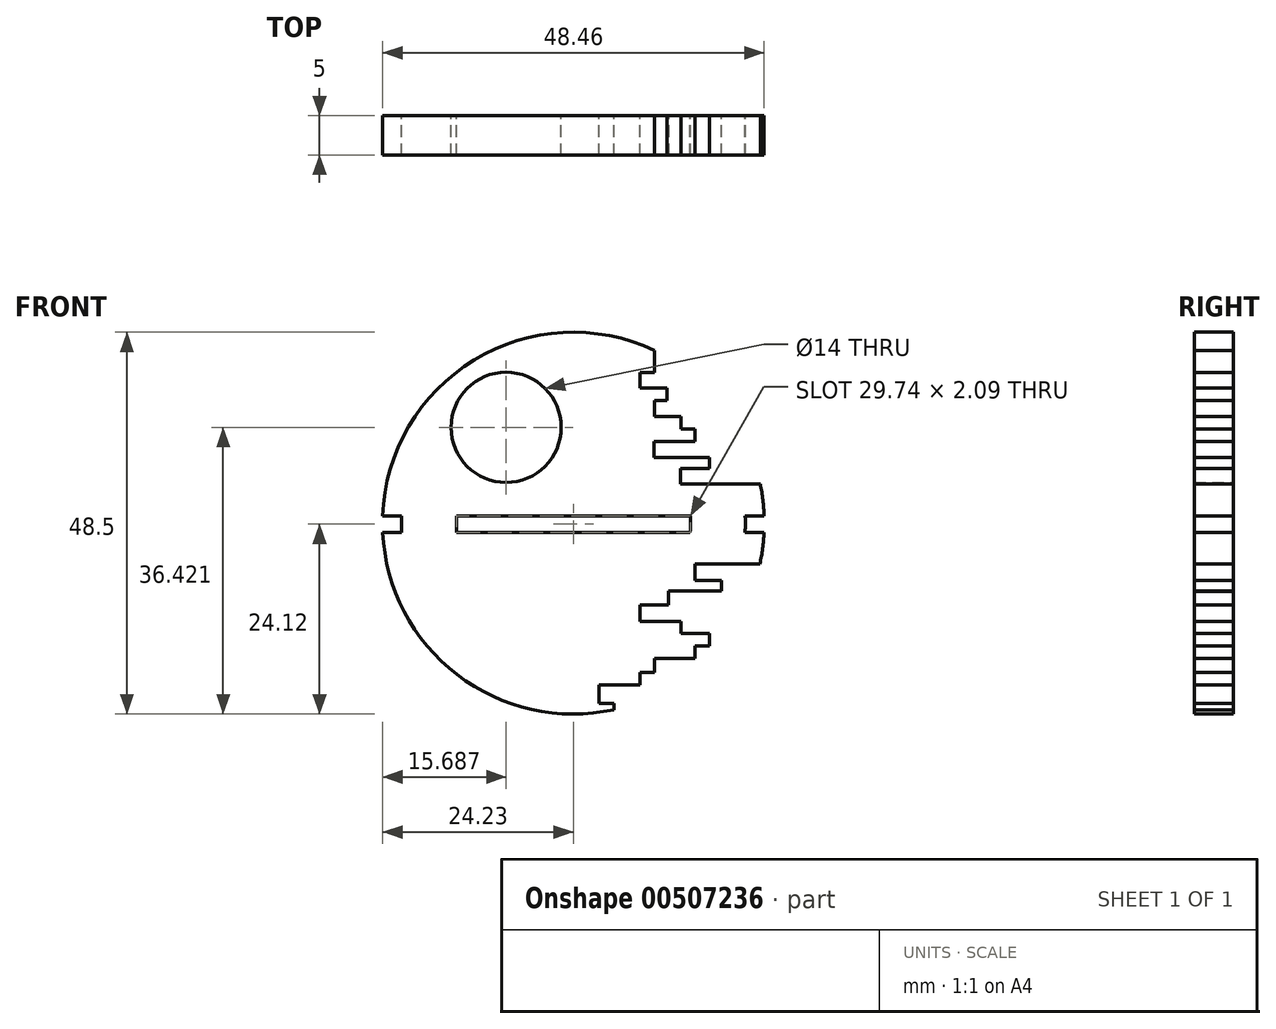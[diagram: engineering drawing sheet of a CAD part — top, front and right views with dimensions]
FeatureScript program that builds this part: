
annotation { "Feature Type Name" : "Feature", "Feature Type Description" : "" }
export const myFeature = defineFeature(function(context is Context, id is Id, definition is map)
    precondition{}
    {
        {
            var Q0;
            Q0=qCreatedBy(makeId("Front.planeOp"),FACE);
            var sketch = newSketch(context, id + "F0", { "sketchPlane" : qUnion([Q0])});
            skLineSegment(sketch, "E0", {"start": v(0, 24.25) * mm, "end": v(0, -24.25) * mm, "construction": true});
            skArc(sketch, "E1", {"start": v(-24.22, -1.17) * mm, "mid": v(-14.76, -19.24) * mm, "end": v(5.13, -23.7) * mm});
            skLineSegment(sketch, "E2", {"start": v(-24.23, 0.91) * mm, "end": v(-21.82, 0.91) * mm});
            skLineSegment(sketch, "E3", {"start": v(24.22, -1.17) * mm, "end": v(21.8, -1.17) * mm});
            skPoint(sketch, "E4.orphan", {"position": v(-3.9, 6.94) * mm});
            skCircle(sketch, "E5", {"center": v(-8.54, 12.17) * mm, "radius": 7 * mm});
            skLineSegment(sketch, "E6", {"start": v(-13.2, 17.4) * mm, "end": v(-8.54, 12.17) * mm, "construction": true});
            skArc(sketch, "E7.trimOffspring", {"start": v(24.23, 0.91) * mm, "mid": v(24.07, 2.95) * mm, "end": v(23.74, 4.96) * mm});
            skPoint(sketch, "E8.orphan", {"position": v(24.25, 0) * mm});
            skPoint(sketch, "E9.start.orphan", {"position": v(-24.25, 0) * mm});
            skLineSegment(sketch, "E10", {"start": v(5.13, -23.7) * mm, "end": v(5.13, -22.88) * mm});
            skLineSegment(sketch, "E11", {"start": v(5.13, -22.88) * mm, "end": v(3.26, -22.88) * mm});
            skLineSegment(sketch, "E12", {"start": v(3.26, -22.88) * mm, "end": v(3.26, -20.54) * mm});
            skLineSegment(sketch, "E13", {"start": v(3.26, -20.54) * mm, "end": v(8.46, -20.54) * mm});
            skLineSegment(sketch, "E14", {"start": v(8.46, -20.54) * mm, "end": v(8.46, -18.97) * mm});
            skLineSegment(sketch, "E15", {"start": v(8.46, -18.97) * mm, "end": v(10.29, -18.97) * mm});
            skLineSegment(sketch, "E16", {"start": v(10.29, -18.97) * mm, "end": v(10.29, -17.2) * mm});
            skLineSegment(sketch, "E17", {"start": v(10.29, -17.2) * mm, "end": v(15.45, -17.2) * mm});
            skLineSegment(sketch, "E18", {"start": v(15.45, -17.2) * mm, "end": v(15.45, -15.6) * mm});
            skLineSegment(sketch, "E19", {"start": v(15.45, -15.6) * mm, "end": v(17.29, -15.6) * mm});
            skLineSegment(sketch, "E20", {"start": v(17.29, -15.6) * mm, "end": v(17.29, -14.02) * mm});
            skLineSegment(sketch, "E21", {"start": v(17.29, -14.02) * mm, "end": v(13.64, -14.02) * mm});
            skLineSegment(sketch, "E22", {"start": v(13.64, -14.02) * mm, "end": v(13.64, -12.47) * mm});
            skLineSegment(sketch, "E23", {"start": v(13.64, -12.47) * mm, "end": v(8.45, -12.47) * mm});
            skLineSegment(sketch, "E24", {"start": v(8.45, -12.47) * mm, "end": v(8.45, -10.39) * mm});
            skLineSegment(sketch, "E25", {"start": v(8.45, -10.39) * mm, "end": v(12.08, -10.39) * mm});
            skLineSegment(sketch, "E26", {"start": v(12.08, -10.39) * mm, "end": v(12.08, -8.59) * mm});
            skLineSegment(sketch, "E27", {"start": v(12.08, -8.59) * mm, "end": v(18.83, -8.59) * mm});
            skLineSegment(sketch, "E28", {"start": v(18.83, -8.59) * mm, "end": v(18.83, -7.28) * mm});
            skLineSegment(sketch, "E29", {"start": v(18.83, -7.28) * mm, "end": v(15.46, -7.28) * mm});
            skLineSegment(sketch, "E30", {"start": v(15.46, -7.28) * mm, "end": v(15.46, -5.2) * mm});
            skLineSegment(sketch, "E31", {"start": v(15.46, -5.2) * mm, "end": v(23.69, -5.2) * mm});
            skLineSegment(sketch, "E32", {"start": v(23.74, 4.96) * mm, "end": v(13.63, 4.96) * mm});
            skLineSegment(sketch, "E33", {"start": v(13.63, 4.96) * mm, "end": v(13.63, 6.96) * mm});
            skLineSegment(sketch, "E34", {"start": v(13.63, 6.96) * mm, "end": v(17.3, 6.96) * mm});
            skLineSegment(sketch, "E35", {"start": v(17.3, 6.96) * mm, "end": v(17.3, 8.31) * mm});
            skLineSegment(sketch, "E36", {"start": v(17.3, 8.31) * mm, "end": v(10.26, 8.31) * mm});
            skLineSegment(sketch, "E37", {"start": v(10.26, 8.31) * mm, "end": v(10.26, 10.38) * mm});
            skLineSegment(sketch, "E38", {"start": v(10.26, 10.38) * mm, "end": v(15.46, 10.38) * mm});
            skLineSegment(sketch, "E39", {"start": v(15.46, 10.38) * mm, "end": v(15.46, 11.97) * mm});
            skLineSegment(sketch, "E40", {"start": v(15.46, 11.97) * mm, "end": v(13.68, 11.97) * mm});
            skLineSegment(sketch, "E41", {"start": v(13.68, 11.97) * mm, "end": v(13.68, 13.53) * mm});
            skLineSegment(sketch, "E42", {"start": v(13.68, 13.53) * mm, "end": v(10.29, 13.53) * mm});
            skLineSegment(sketch, "E43", {"start": v(10.29, 13.53) * mm, "end": v(10.29, 15.59) * mm});
            skLineSegment(sketch, "E44", {"start": v(10.29, 15.59) * mm, "end": v(11.87, 15.59) * mm});
            skLineSegment(sketch, "E45", {"start": v(11.87, 15.59) * mm, "end": v(11.87, 17.18) * mm});
            skLineSegment(sketch, "E46", {"start": v(11.87, 17.18) * mm, "end": v(8.45, 17.18) * mm});
            skLineSegment(sketch, "E47", {"start": v(8.45, 17.18) * mm, "end": v(8.45, 19.14) * mm});
            skLineSegment(sketch, "E48", {"start": v(8.45, 19.14) * mm, "end": v(10.29, 19.14) * mm});
            skLineSegment(sketch, "E49", {"start": v(10.29, 19.14) * mm, "end": v(10.29, 21.96) * mm});
            skArc(sketch, "E50", {"start": v(21.8, -1.17) * mm, "mid": v(21.84, -0.13) * mm, "end": v(21.82, 0.91) * mm});
            skArc(sketch, "E51", {"start": v(-14.84, 0.91) * mm, "mid": v(-14.87, -0.13) * mm, "end": v(-14.82, -1.17) * mm});
            skArc(sketch, "E52.trimOffspring", {"start": v(14.82, -1.17) * mm, "mid": v(14.87, -0.13) * mm, "end": v(14.84, 0.91) * mm});
            skArc(sketch, "E53.trimOffspring", {"start": v(12.08, -8.67) * mm, "mid": v(12.11, -8.63) * mm, "end": v(12.14, -8.59) * mm});
            skArc(sketch, "E54.trimOffspring", {"start": v(-11.89, 18.32) * mm, "mid": v(-12.55, 17.88) * mm, "end": v(-13.2, 17.4) * mm});
            skArc(sketch, "E55.trimOffspring", {"start": v(-21.82, 0.91) * mm, "mid": v(-21.84, -0.13) * mm, "end": v(-21.8, -1.17) * mm});
            skLineSegment(sketch, "E56.trimOffspring", {"start": v(21.82, 0.91) * mm, "end": v(24.23, 0.91) * mm});
            skLineSegment(sketch, "E57.trimOffspring", {"start": v(14.82, -1.17) * mm, "end": v(-14.82, -1.17) * mm});
            skLineSegment(sketch, "E58.trimOffspring", {"start": v(-21.8, -1.17) * mm, "end": v(-24.23, -1.17) * mm});
            skLineSegment(sketch, "E59.trimOffspring", {"start": v(-14.84, 0.91) * mm, "end": v(14.84, 0.91) * mm});
            skArc(sketch, "E60.trimOffspring", {"start": v(10.29, 21.96) * mm, "mid": v(-12.62, 20.7) * mm, "end": v(-24.23, 0.91) * mm});
            skArc(sketch, "E61.trimOffspring", {"start": v(23.69, -5.2) * mm, "mid": v(24.04, -3.2) * mm, "end": v(24.22, -1.17) * mm});
            skSolve(sketch);
        }
        {
            var Q0;
            Q0 = qSketchRegion(id + "F0", true);
            extrude(context, id + "F1", {"entities" : qUnion([Q0]), "depth" : 5 * mm});
        }
    });
